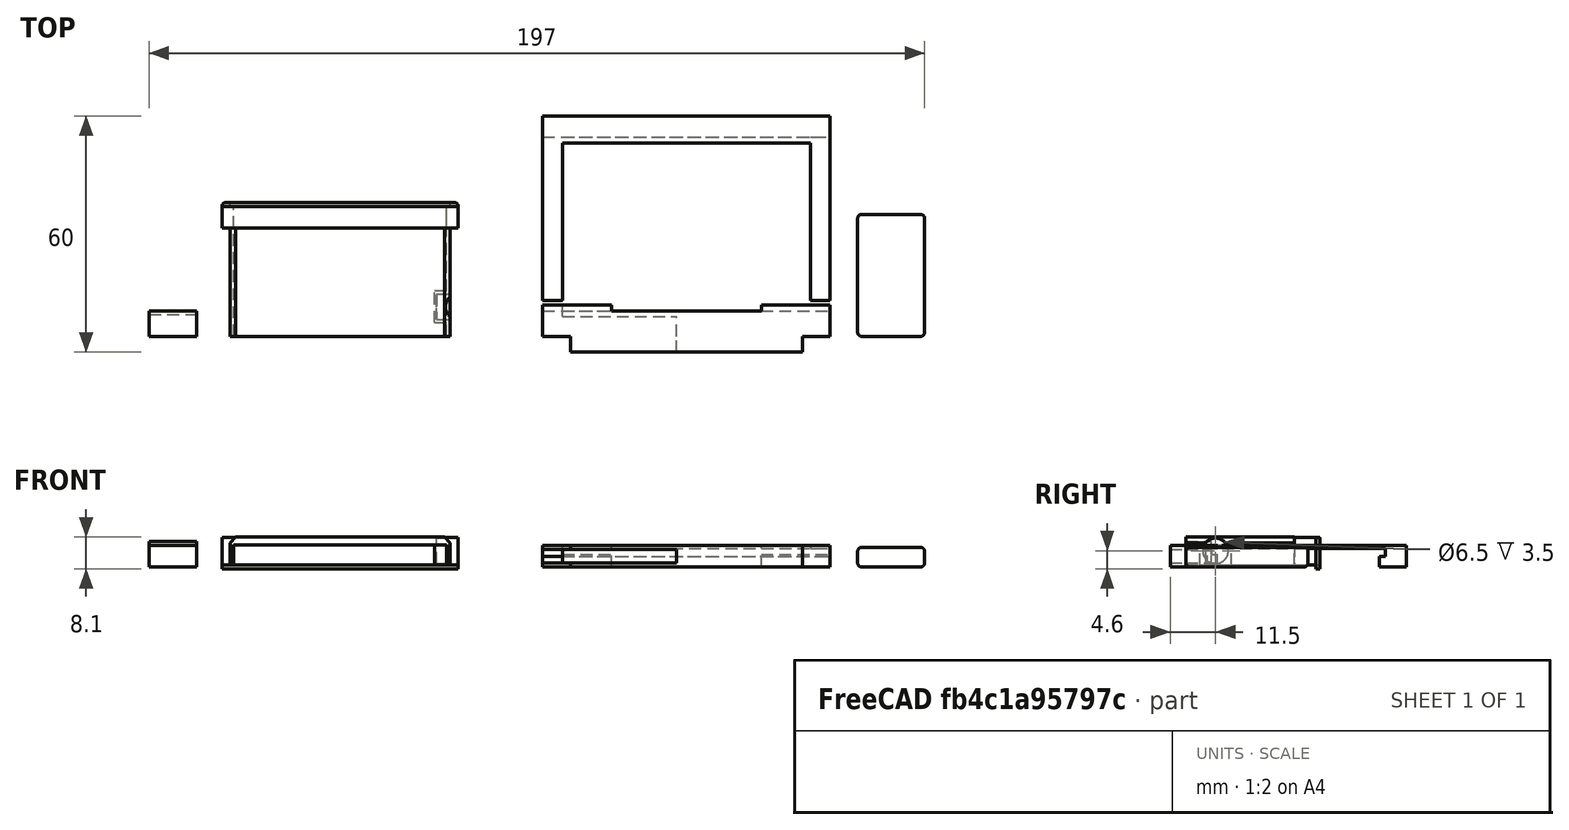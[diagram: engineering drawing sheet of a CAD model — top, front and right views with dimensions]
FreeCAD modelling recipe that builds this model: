
FCSTD DOCUMENT  (FreeCAD 0.18R16131 (Git))
Label: ardubigboy
License: All rights reserved
LicenseURL: http://en.wikipedia.org/wiki/All_rights_reserved
objects: Part::Box×22, Part::Cut×9, Part::MultiFuse×5, Part::Fillet×3, Part::Chamfer×1, Part::Cylinder×1
note: 41 computed .brp shape members not serialized (recipe doc carries the construction recipe); baked Part::Feature solids carry a one-line shape summary decoded from their .brp

FEATURE [Part::Box] Box001  label="Cube(screen_surround_buttom)"
  AttacherType = Attacher::AttachEngine3D
  Height = 5.5
  Length = 73
  Width = 6.5
FEATURE [Part::Box] Box002  label="Cube(under_screen_surround)"
  AttacherType = Attacher::AttachEngine3D
  Height = 5.5
  Length = 59
  Placement = pos=(7,-4,0) rot=(0,0,1;0rad)
  Width = 4
FEATURE [Part::Box] Box005  label="Cube(screen_surround_top)"
  AttacherType = Attacher::AttachEngine3D
  Height = 5.5
  Length = 73
  Placement = pos=(0,50.65,0) rot=(0,0,1;0rad)
  Width = 5.35
FEATURE [Part::Box] Box007  label="Cube(screen_surround_top_groove_outer)"
  AttacherType = Attacher::AttachEngine3D
  Height = 5.5
  Length = 73
  Placement = pos=(0,49.15,0) rot=(0,0,1;0rad)
  Width = 1.5
FEATURE [Part::Box] Box008  label="Cube(screen_surround_top_groove_inner)"
  AttacherType = Attacher::AttachEngine3D
  Height = 2
  Length = 73
  Placement = pos=(0,49.15,2.7) rot=(0,0,1;0rad)
  Width = 1.5
FEATURE [Part::Box] Box009  label="Cube(screen_surround_bottom_groove_outer)"
  AttacherType = Attacher::AttachEngine3D
  Height = 5.5
  Length = 73
  Placement = pos=(0,6.5,0) rot=(0,0,1;0rad)
  Width = 1.5
FEATURE [Part::Box] Box010  label="Cube(screen_surround_bottom_groove_inner)"
  AttacherType = Attacher::AttachEngine3D
  Height = 1.5
  Length = 73
  Placement = pos=(0,6.5,3.2) rot=(0,0,1;0rad)
  Width = 1.5
FEATURE [Part::Box] Box011  label="Cube(screen_surround_bottom_groove_middle_cut)"
  AttacherType = Attacher::AttachEngine3D
  Height = 5.5
  Length = 38
  Placement = pos=(17.5,6.5,0) rot=(0,0,1;0rad)
  Width = 1.5
FEATURE [Part::MultiFuse] Fusion
  Shapes = -> [Box002,Box001,Box009]
FEATURE [Part::Cut] Cut
  Base = -> Fusion
  Tool = -> Box011
FEATURE [Part::MultiFuse] Fusion001
  Shapes = -> [Box005,Box007]
FEATURE [Part::Cut] Cut002
  Base = -> Fusion001
  Tool = -> Box008
FEATURE [Part::Box] Box012  label="Cube(front_cover_left)"
  AttacherType = Attacher::AttachEngine3D
  Height = 0.8
  Length = 5
  Placement = pos=(0,9.15,4.7) rot=(0,0,1;0rad)
  Width = 41.5
FEATURE [Part::Box] Box013  label="Cube(front_cover_right)"
  AttacherType = Attacher::AttachEngine3D
  Height = 0.8
  Length = 5
  Placement = pos=(68,9.15,4.7) rot=(0,0,1;0rad)
  Width = 41.5
FEATURE [Part::Box] Box014  label="Cube(wire_cutter_left)"
  AttacherType = Attacher::AttachEngine3D
  Height = 3.5
  Length = 5
  Placement = pos=(0,0,1) rot=(0,0,1;0rad)
  Width = 8
FEATURE [Part::Box] Box015  label="Cube001(wire_cutter_left_bottom)"
  AttacherType = Attacher::AttachEngine3D
  Height = 3.5
  Length = 34
  Placement = pos=(0,0,1) rot=(0,0,1;0rad)
  Width = 5
FEATURE [Part::Box] Box016  label="Cube002(wire_cutter_bottom)"
  AttacherType = Attacher::AttachEngine3D
  Height = 3.5
  Length = 27
  Placement = pos=(7,-4,1) rot=(0,0,1;0rad)
  Width = 4
FEATURE [Part::Cut] Cut003
  Base = -> Cut
  Tool = -> Box010
FEATURE [Part::Cut] Cut004
  Base = -> Cut003
  Tool = -> Box014
FEATURE [Part::Cut] Cut005
  Base = -> Cut004
  Tool = -> Box016
FEATURE [Part::MultiFuse] Fusion002
  Shapes = -> [Cut002,Box012,Box013]
FEATURE [Part::Cut] Cut006
  Base = -> Cut005
  Tool = -> Box015
FEATURE [Part::Box] Box  label="Cube(outer)"
  AttacherType = Attacher::AttachEngine3D
  Height = 5.1
  Length = 56
  Placement = pos=(-79.5,0,0.5) rot=(0,0,1;0rad)
  Width = 34
FEATURE [Part::Box] Box017  label="Cube(inner)"
  AttacherType = Attacher::AttachEngine3D
  Height = 5.1
  Length = 54
  Placement = pos=(-78.5,0,0.5) rot=(0,0,1;0rad)
  Width = 33
FEATURE [Part::Box] Box025  label="Cube001"
  AttacherType = Attacher::AttachEngine3D
  Height = 2
  Length = 56
  Placement = pos=(-79.5,0,5.6) rot=(0,0,1;0rad)
  Width = 27.5
FEATURE [Part::Box] Box026  label="Cube002(lid_top)"
  AttacherType = Attacher::AttachEngine3D
  Height = 7
  Length = 60
  Placement = pos=(-81.5,27.5,0.5) rot=(0,0,1;0rad)
  Width = 5.5
FEATURE [Part::Chamfer] Chamfer
  Base = -> Box025
  Edges = 2 edges r=1.5: [Edge2,Edge6]
FEATURE [Part::Cylinder] Cylinder005  label="Cylinder003(magnet)"
  Angle = 360
  AttacherType = Attacher::AttachEngine3D
  Height = 3.5
  Placement = pos=(-27,7.5,4.1) rot=(0,1,0;1.5708rad)
  Radius = 3.25
FEATURE [Part::Box] Box043  label="Cube010(magnet_back)"
  AttacherType = Attacher::AttachEngine3D
  Height = 5.5
  Length = 3
  Placement = pos=(-27.5,3.5,0.5) rot=(0,0,1;0rad)
  Width = 8
FEATURE [Part::Box] Box044  label="Cube011(battery_shim)"
  AttacherType = Attacher::AttachEngine3D
  Height = 5
  Length = 17
  Placement = pos=(80,0,0) rot=(0,0,1;0rad)
  Width = 31
FEATURE [Part::Fillet] Fillet007  label="Fillet007(battery_shim)"
  Base = -> Box044
  Edges = 12 edges r=1: [Edge1,Edge2,Edge3,Edge4,Edge5,Edge6,Edge7,Edge8,Edge9,Edge10,Edge11,Edge12]
FEATURE [Part::Box] Box045  label="Cube011(port_cover_outer)"
  AttacherType = Attacher::AttachEngine3D
  Height = 6.5
  Length = 12
  Placement = pos=(-100,0,0) rot=(0,0,1;0rad)
  Width = 6.5
FEATURE [Part::Box] Box046  label="Cube011(port_cover_inner)"
  AttacherType = Attacher::AttachEngine3D
  Height = 5.5
  Length = 12
  Placement = pos=(-100,0,0) rot=(0,0,1;0rad)
  Width = 5.5
FEATURE [Part::Cut] Cut032  label="Cut032(port_cover)"
  Base = -> Box045
  Tool = -> Box046
FEATURE [Part::Box] Box047  label="Cube002(lid_top_top)"
  AttacherType = Attacher::AttachEngine3D
  Height = 8
  Length = 60
  Placement = pos=(-81.5,33,-0.5) rot=(0,0,1;0rad)
  Width = 1
FEATURE [Part::MultiFuse] Fusion003
  Shapes = -> [Chamfer,Box026,Box]
FEATURE [Part::Cut] Cut033
  Base = -> Fusion003
  Tool = -> Box017
FEATURE [Part::MultiFuse] Fusion004
  Shapes = -> [Cut033,Box043]
FEATURE [Part::Cut] Cut034
  Base = -> Fusion004
  Tool = -> Cylinder005
FEATURE [Part::Fillet] Fillet
  Base = -> Box047
  Edges = 1 edges r=0.9: [Edge3]
FEATURE [Part::Fillet] Fillet008
  Base = -> Fillet
  Edges = 1 edges r=0.9: [Edge15]
